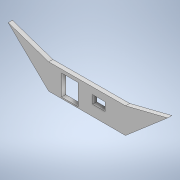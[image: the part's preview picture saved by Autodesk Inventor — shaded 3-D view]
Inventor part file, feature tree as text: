
AUTODESK INVENTOR PART (.ipt)
format: ipt  version: 2020.1 (Build 241239000, 239)  size: 121,344 bytes
history: native  units: in
note: dims shown in document units (in); Inventor stores cm internally (conversion verified against a paired STEP export)
features: extrude x1, sketch x1
ambient origin geometry x8: Origin, YZ Plane, XZ Plane, XY Plane, X Axis, Y Axis, Z Axis, Center Point
bodies: Solid1 (feature_tree)
feature tree (2):
  extrude  "Extrusion1"  Depth=48.0in
  sketch  "Sketch1"  dims[d2=221.0in d5=48.0in d6=60.0in d8=162.0in d11=73.0in d12=123.0in d13=74.0in d14=160.0in d15=125.0in d16=36.0in d17=24.0in d18=12.0in d19=0.0in]
